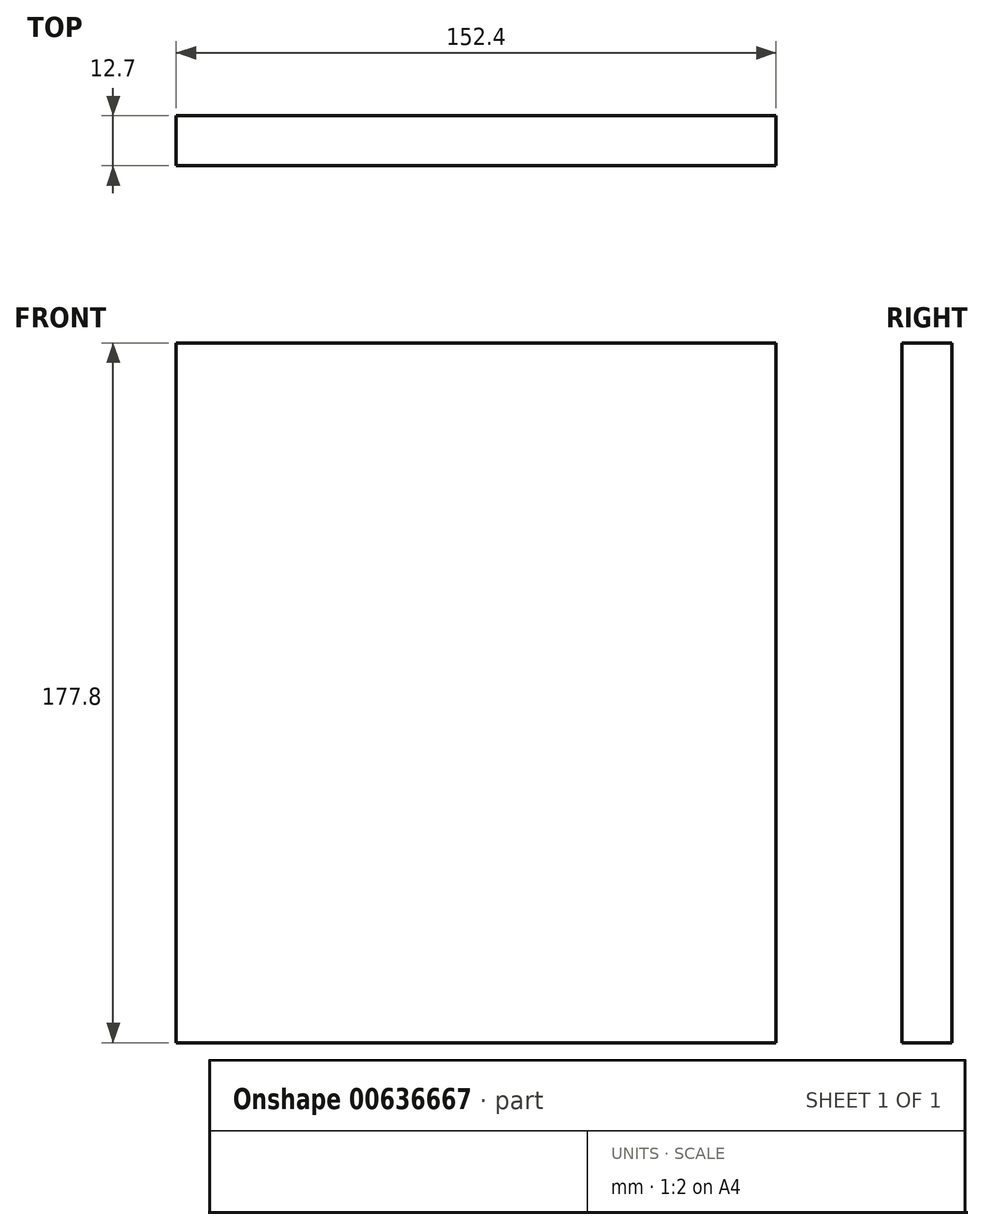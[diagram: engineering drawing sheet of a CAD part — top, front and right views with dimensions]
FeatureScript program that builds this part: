
annotation { "Feature Type Name" : "Feature", "Feature Type Description" : "" }
export const myFeature = defineFeature(function(context is Context, id is Id, definition is map)
    precondition{}
    {
        {
            var Q0;
            Q0=qCreatedBy(makeId("Front.planeOp"),FACE);
            var sketch = newSketch(context, id + "F0", { "sketchPlane" : qUnion([Q0])});
            skLineSegment(sketch, "E0.bottom", {"start": v(-56.63, 122.1) * mm, "end": v(95.77, 122.1) * mm});
            skLineSegment(sketch, "E0.top", {"start": v(-56.63, -55.7) * mm, "end": v(95.77, -55.7) * mm});
            skLineSegment(sketch, "E0.left", {"start": v(-56.63, 122.1) * mm, "end": v(-56.63, -55.7) * mm});
            skLineSegment(sketch, "E0.right", {"start": v(95.77, 122.1) * mm, "end": v(95.77, -55.7) * mm});
            skSolve(sketch);
        }
        {
            var Q0;
            Q0=makeQuery(id+"F0.imprint","IMPRINT",FACE,{"disambiguationData":[TD([[makeQuery(id+"F0.imprint","IMPRINT",EDGE,{"derivedFrom":sQuery(id+"F0.wireOp",EDGE,"E0.bottom")}),-1.0]])]});
            extrude(context, id + "F1", {"entities" : qUnion([Q0]), "depth" : 12.7 * mm, "offsetDistance" : 25.4 * mm});
        }
    });
